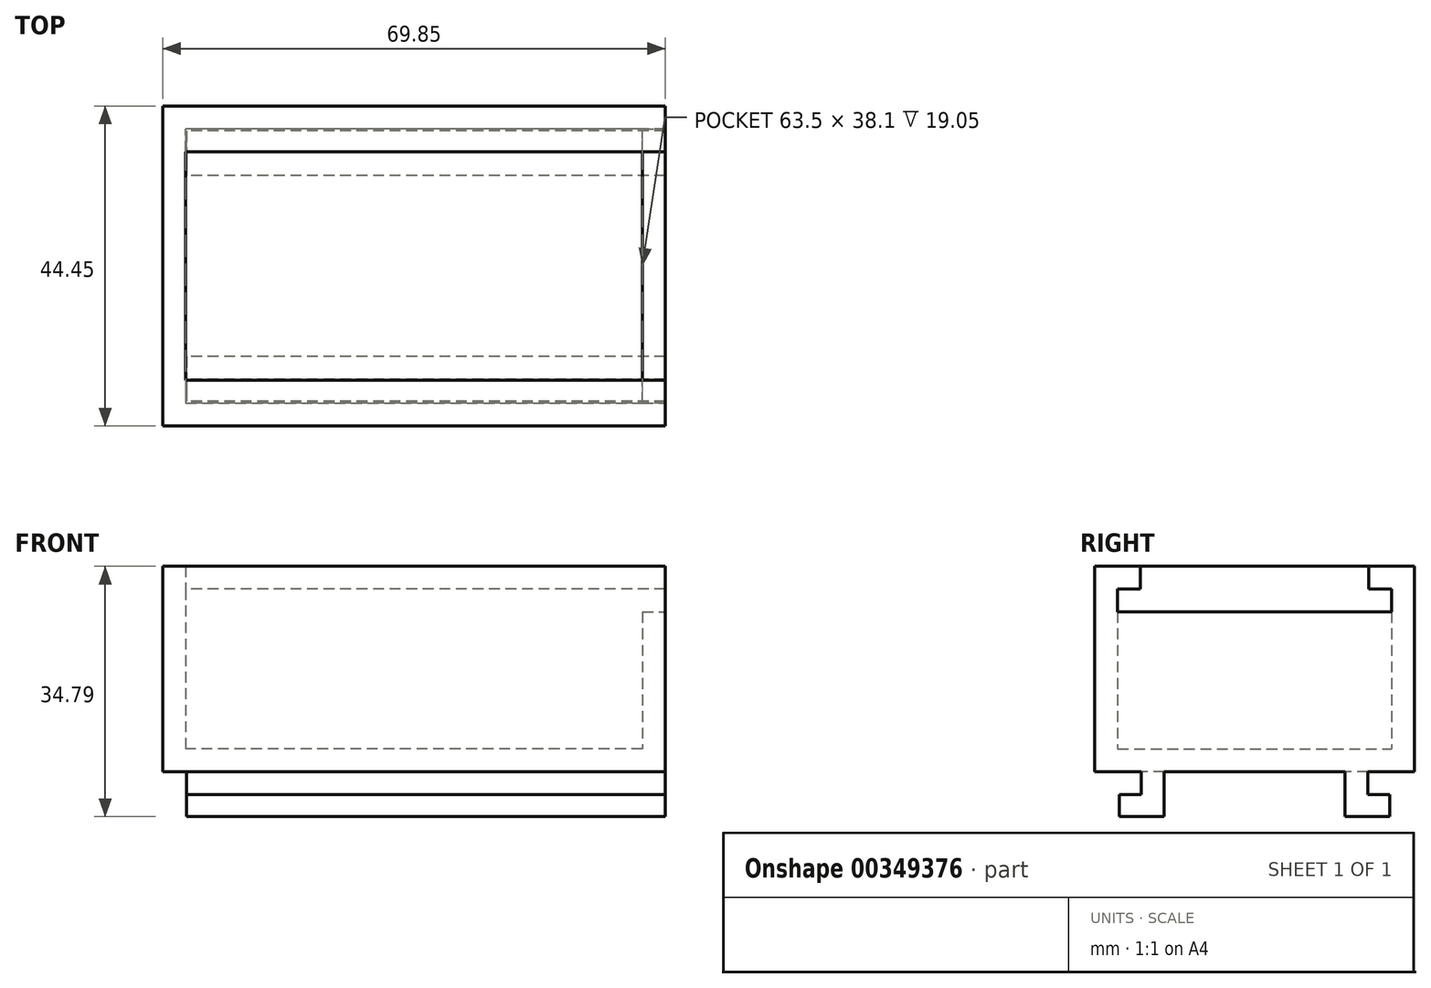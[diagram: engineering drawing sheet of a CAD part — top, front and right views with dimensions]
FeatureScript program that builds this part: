
annotation { "Feature Type Name" : "Feature", "Feature Type Description" : "" }
export const myFeature = defineFeature(function(context is Context, id is Id, definition is map)
    precondition{}
    {
        {
            var Q0;
            Q0=qCreatedBy(makeId("Top.planeOp"),FACE);
            var sketch = newSketch(context, id + "F0", { "sketchPlane" : qUnion([Q0])});
            skLineSegment(sketch, "E0.bottom", {"start": v(0, 0) * mm, "end": v(69.85, 0) * mm});
            skLineSegment(sketch, "E0.top", {"start": v(0, 44.45) * mm, "end": v(69.85, 44.45) * mm});
            skLineSegment(sketch, "E0.left", {"start": v(0, 0) * mm, "end": v(0, 44.45) * mm});
            skLineSegment(sketch, "E0.right", {"start": v(69.85, 0) * mm, "end": v(69.85, 44.45) * mm});
            skSolve(sketch);
        }
        {
            var Q0;
            Q0=makeQuery(id+"F0.imprint","IMPRINT",FACE,{"disambiguationData":[TD([[makeQuery(id+"F0.imprint","IMPRINT",EDGE,{"derivedFrom":sQuery(id+"F0.wireOp",EDGE,"E0.bottom")}),1.0]])]});
            extrude(context, id + "F1", {"entities" : qUnion([Q0]), "depth" : 3.17 * mm});
        }
        {
            var Q0;
            Q0=makeQuery(id+"F1.opExtrude","CAP_FACE",FACE,{"disambiguationData":[OSD([sQuery(id+"F0.wireOp",EDGE,"E0.bottom"),sQuery(id+"F0.wireOp",EDGE,"E0.top"),sQuery(id+"F0.wireOp",EDGE,"E0.left"),sQuery(id+"F0.wireOp",EDGE,"E0.right")])],"isStart":false});
            var sketch = newSketch(context, id + "F2", { "sketchPlane" : qUnion([Q0])});
            skLineSegment(sketch, "E1.0", {"start": v(66.67, 41.27) * mm, "end": v(3.17, 41.27) * mm});
            skLineSegment(sketch, "E1.1", {"start": v(66.67, 3.17) * mm, "end": v(66.67, 41.27) * mm});
            skLineSegment(sketch, "E1.2", {"start": v(3.17, 3.17) * mm, "end": v(66.67, 3.17) * mm});
            skLineSegment(sketch, "E1.3", {"start": v(3.17, 41.27) * mm, "end": v(3.17, 3.17) * mm});
            skSolve(sketch);
        }
        {
            var Q0;
            Q0=makeQuery(id+"F2.imprint","IMPRINT",FACE,{"disambiguationData":[TD([[makeQuery(id+"F2.imprint","IMPRINT",EDGE,{"derivedFrom":sQuery(id+"F2.wireOp",EDGE,"E1.0")}),-1.0]])]});
            extrude(context, id + "F3", {"entities" : qUnion([Q0]), "operationType" : NewBodyOperationType.ADD, "depth" : 25.4 * mm});
        }
        {
            var Q0;
            Q0=makeQuery(id+"F1.opExtrude","CAP_FACE",FACE,{"disambiguationData":[OSD([sQuery(id+"F0.wireOp",EDGE,"E0.bottom"),sQuery(id+"F0.wireOp",EDGE,"E0.top"),sQuery(id+"F0.wireOp",EDGE,"E0.left"),sQuery(id+"F0.wireOp",EDGE,"E0.right")])],"isStart":true});
            var sketch = newSketch(context, id + "F4", { "sketchPlane" : qUnion([Q0])});
            skLineSegment(sketch, "E2.bottom", {"start": v(69.85, -6.48) * mm, "end": v(0, -6.48) * mm});
            skLineSegment(sketch, "E2.top", {"start": v(69.85, -9.65) * mm, "end": v(0, -9.65) * mm});
            skLineSegment(sketch, "E2.left", {"start": v(69.85, -6.48) * mm, "end": v(69.85, -9.65) * mm});
            skLineSegment(sketch, "E2.right", {"start": v(0, -6.48) * mm, "end": v(0, -9.65) * mm});
            skLineSegment(sketch, "E3", {"start": v(69.85, -22.22) * mm, "end": v(0, -22.22) * mm});
            skLineSegment(sketch, "E4.MirrorCS", {"start": v(69.85, -34.8) * mm, "end": v(0, -34.8) * mm});
            skLineSegment(sketch, "E5.MirrorCS", {"start": v(69.85, -37.97) * mm, "end": v(69.85, -34.8) * mm});
            skLineSegment(sketch, "E6.MirrorCS", {"start": v(69.85, -37.97) * mm, "end": v(0, -37.97) * mm});
            skLineSegment(sketch, "E7.MirrorCS", {"start": v(0, -37.97) * mm, "end": v(0, -34.8) * mm});
            skSolve(sketch);
        }
        {
            var Q0;
            Q0 = qSketchRegion(id + "F4", true);
            extrude(context, id + "F5", {"entities" : qUnion([Q0]), "operationType" : NewBodyOperationType.ADD, "depth" : 6.22 * mm});
        }
        {
            var Q0;
            Q0=makeQuery(id+"F5.opExtrude","SWEPT_FACE",FACE,{"disambiguationData":[OSD([sQuery(id+"F4.wireOp",EDGE,"E2.bottom")])]});
            var sketch = newSketch(context, id + "F6", { "sketchPlane" : qUnion([Q0])});
            skLineSegment(sketch, "E8.bottom", {"start": v(69.85, -6.22) * mm, "end": v(0, -6.22) * mm});
            skLineSegment(sketch, "E8.top", {"start": v(69.85, -3.18) * mm, "end": v(0, -3.18) * mm});
            skLineSegment(sketch, "E8.left", {"start": v(69.85, -6.22) * mm, "end": v(69.85, -3.18) * mm});
            skLineSegment(sketch, "E8.right", {"start": v(0, -6.22) * mm, "end": v(0, -3.18) * mm});
            skSolve(sketch);
        }
        {
            var Q0;
            Q0=makeQuery(id+"F6.imprint","IMPRINT",FACE,{"disambiguationData":[TD([[makeQuery(id+"F6.imprint","IMPRINT",EDGE,{"derivedFrom":sQuery(id+"F6.wireOp",EDGE,"E8.bottom")}),-1.0]])]});
            extrude(context, id + "F7", {"entities" : qUnion([Q0]), "operationType" : NewBodyOperationType.ADD, "depth" : 3.05 * mm});
        }
        {
            var Q0;
            Q0=makeQuery(id+"F5.opExtrude","SWEPT_FACE",FACE,{"disambiguationData":[OSD([sQuery(id+"F4.wireOp",EDGE,"E6.MirrorCS")])]});
            var sketch = newSketch(context, id + "F8", { "sketchPlane" : qUnion([Q0])});
            skLineSegment(sketch, "E9.bottom", {"start": v(-69.85, -6.22) * mm, "end": v(0, -6.22) * mm});
            skLineSegment(sketch, "E9.top", {"start": v(-69.85, -3.17) * mm, "end": v(0, -3.17) * mm});
            skLineSegment(sketch, "E9.left", {"start": v(-69.85, -6.22) * mm, "end": v(-69.85, -3.17) * mm});
            skLineSegment(sketch, "E9.right", {"start": v(0, -6.22) * mm, "end": v(0, -3.17) * mm});
            skSolve(sketch);
        }
        {
            var Q0;
            Q0=makeQuery(id+"F8.imprint","IMPRINT",FACE,{"disambiguationData":[TD([[makeQuery(id+"F8.imprint","IMPRINT",EDGE,{"derivedFrom":sQuery(id+"F8.wireOp",EDGE,"E9.bottom")}),1.0]])]});
            extrude(context, id + "F9", {"entities" : qUnion([Q0]), "operationType" : NewBodyOperationType.ADD, "depth" : 3.05 * mm});
        }
        {
            var Q0;
            Q0=makeQuery(id+"F3.opExtrude","SWEPT_FACE",FACE,{"disambiguationData":[OSD([sQuery(id+"F2.wireOp",EDGE,"E1.2")])]});
            var sketch = newSketch(context, id + "F10", { "sketchPlane" : qUnion([Q0])});
            skLineSegment(sketch, "E10.bottom", {"start": v(-66.67, 28.58) * mm, "end": v(-3.17, 28.58) * mm});
            skLineSegment(sketch, "E10.top", {"start": v(-66.67, 25.4) * mm, "end": v(-3.17, 25.4) * mm});
            skLineSegment(sketch, "E10.left", {"start": v(-66.67, 28.58) * mm, "end": v(-66.67, 25.4) * mm});
            skLineSegment(sketch, "E10.right", {"start": v(-3.17, 28.58) * mm, "end": v(-3.17, 25.4) * mm});
            skSolve(sketch);
        }
        {
            var Q0;
            Q0=makeQuery(id+"F10.imprint","IMPRINT",FACE,{"disambiguationData":[TD([[makeQuery(id+"F10.imprint","IMPRINT",EDGE,{"derivedFrom":sQuery(id+"F10.wireOp",EDGE,"E10.bottom")}),1.0]])]});
            extrude(context, id + "F11", {"entities" : qUnion([Q0]), "operationType" : NewBodyOperationType.ADD, "depth" : 3.17 * mm});
        }
        {
            var Q0;
            Q0=makeQuery(id+"F3.opExtrude","SWEPT_FACE",FACE,{"disambiguationData":[OSD([sQuery(id+"F2.wireOp",EDGE,"E1.0")])]});
            var sketch = newSketch(context, id + "F12", { "sketchPlane" : qUnion([Q0])});
            skLineSegment(sketch, "E11.bottom", {"start": v(66.67, 28.58) * mm, "end": v(3.17, 28.57) * mm});
            skLineSegment(sketch, "E11.top", {"start": v(66.67, 25.4) * mm, "end": v(3.17, 25.4) * mm});
            skLineSegment(sketch, "E11.left", {"start": v(66.67, 28.58) * mm, "end": v(66.67, 25.4) * mm});
            skLineSegment(sketch, "E11.right", {"start": v(3.17, 28.58) * mm, "end": v(3.17, 25.4) * mm});
            skSolve(sketch);
        }
        {
            var Q0;
            Q0=makeQuery(id+"F12.imprint","IMPRINT",FACE,{"disambiguationData":[TD([[makeQuery(id+"F12.imprint","IMPRINT",EDGE,{"derivedFrom":sQuery(id+"F12.wireOp",EDGE,"E11.bottom")}),1.0]])]});
            extrude(context, id + "F13", {"entities" : qUnion([Q0]), "operationType" : NewBodyOperationType.ADD, "depth" : 3.17 * mm});
        }
        {
            var Q0;
            {var subQ0=sQuery(id+"F0.wireOp",EDGE,"E0.right");Q0=makeQuery(id+"F9.boolean.opBoolean","MERGE",FACE,{"derivedFrom":[makeQuery(id+"F7.boolean.opBoolean","MERGE",FACE,{"derivedFrom":[makeQuery(id+"F5.boolean.opBoolean","MERGE",FACE,{"derivedFrom":[makeQuery(id+"F3.boolean.opBoolean","MERGE",FACE,{"derivedFrom":[makeQuery(id+"F1.opExtrude","SWEPT_FACE",FACE,{"disambiguationData":[OSD([subQ0])]}),makeQuery(id+"F3.opExtrude","SWEPT_FACE",FACE,{"disambiguationData":[OSD([subQ0])]})]}),makeQuery(id+"F5.opExtrude","SWEPT_FACE",FACE,{"disambiguationData":[OSD([sQuery(id+"F4.wireOp",EDGE,"E2.left")])]}),makeQuery(id+"F5.opExtrude","SWEPT_FACE",FACE,{"disambiguationData":[OSD([sQuery(id+"F4.wireOp",EDGE,"E5.MirrorCS")])]})]}),makeQuery(id+"F7.opExtrude","SWEPT_FACE",FACE,{"disambiguationData":[OSD([sQuery(id+"F6.wireOp",EDGE,"E8.left")])]})]}),makeQuery(id+"F9.opExtrude","SWEPT_FACE",FACE,{"disambiguationData":[OSD([sQuery(id+"F8.wireOp",EDGE,"E9.left")])]})]});}
            var sketch = newSketch(context, id + "F14", { "sketchPlane" : qUnion([Q0])});
            skLineSegment(sketch, "E12.bottom", {"start": v(6.35, 28.58) * mm, "end": v(38.1, 28.58) * mm});
            skLineSegment(sketch, "E12.top", {"start": v(6.35, 25.4) * mm, "end": v(38.1, 25.4) * mm});
            skLineSegment(sketch, "E12.left", {"start": v(6.35, 28.58) * mm, "end": v(6.35, 25.4) * mm});
            skLineSegment(sketch, "E12.right", {"start": v(38.1, 28.58) * mm, "end": v(38.1, 25.4) * mm});
            skLineSegment(sketch, "E13.bottom", {"start": v(3.18, 25.4) * mm, "end": v(41.27, 25.4) * mm});
            skLineSegment(sketch, "E13.top", {"start": v(3.17, 22.22) * mm, "end": v(41.27, 22.22) * mm});
            skLineSegment(sketch, "E13.left", {"start": v(3.18, 25.4) * mm, "end": v(3.18, 22.22) * mm});
            skLineSegment(sketch, "E13.right", {"start": v(41.27, 25.4) * mm, "end": v(41.27, 22.22) * mm});
            skSolve(sketch);
        }
        {
            var Q0;
            Q0=makeQuery(id+"F14.imprint","IMPRINT",FACE,{"disambiguationData":[TD([[makeQuery(id+"F14.imprint","IMPRINT",EDGE,{"derivedFrom":sQuery(id+"F14.wireOp",EDGE,"E13.top")}),1.0]])]});
            var Q1;
            Q1=makeQuery(id+"F14.imprint","IMPRINT",FACE,{"disambiguationData":[TD([[makeQuery(id+"F14.imprint","IMPRINT",EDGE,{"derivedFrom":sQuery(id+"F14.wireOp",EDGE,"E12.bottom")}),-1.0]])]});
            extrude(context, id + "F15", {"entities" : qUnion([Q0, Q1]), "operationType" : NewBodyOperationType.REMOVE, "endBound" : BoundingType.UP_TO_NEXT, "oppositeDirection" : true, "depth" : 25.4 * mm});
        }
        {
            var Q0;
            Q0=makeQuery(id+"F7.opExtrude","CAP_FACE",FACE,{"disambiguationData":[OSD([sQuery(id+"F6.wireOp",EDGE,"E8.bottom"),sQuery(id+"F6.wireOp",EDGE,"E8.top"),sQuery(id+"F6.wireOp",EDGE,"E8.left"),sQuery(id+"F6.wireOp",EDGE,"E8.right")])],"isStart":false});
            var sketch = newSketch(context, id + "F16", { "sketchPlane" : qUnion([Q0])});
            skLineSegment(sketch, "E14.bottom", {"start": v(0, -6.22) * mm, "end": v(3.3, -6.22) * mm});
            skLineSegment(sketch, "E14.top", {"start": v(0, 0) * mm, "end": v(3.3, 0) * mm});
            skLineSegment(sketch, "E14.left", {"start": v(0, -6.22) * mm, "end": v(0, 0) * mm});
            skLineSegment(sketch, "E14.right", {"start": v(3.3, -6.22) * mm, "end": v(3.3, 0) * mm});
            skSolve(sketch);
        }
        {
            var Q0;
            Q0 = qSketchRegion(id + "F16", true);
            extrude(context, id + "F17", {"entities" : qUnion([Q0]), "operationType" : NewBodyOperationType.REMOVE, "oppositeDirection" : true, "depth" : 38.1 * mm});
        }
    });
